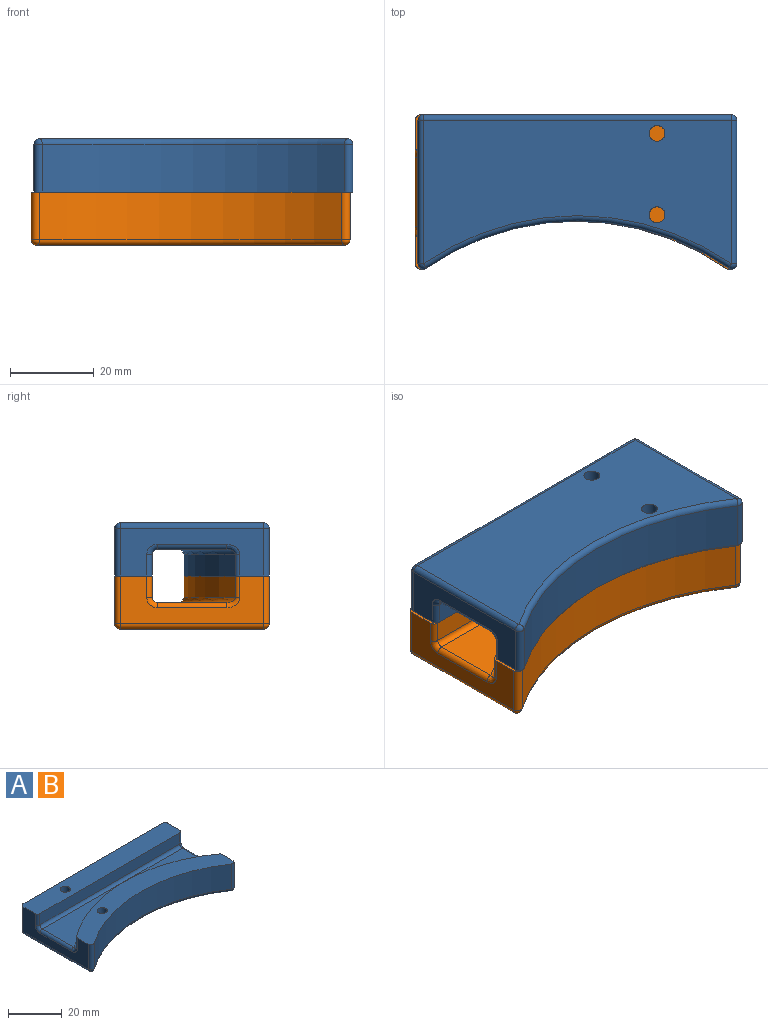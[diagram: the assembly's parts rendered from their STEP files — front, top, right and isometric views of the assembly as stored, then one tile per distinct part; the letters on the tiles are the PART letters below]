
ASSEMBLY  parts=2 mates=1
PART A: 36 faces, bbox 84.1x36.9x12.7 mm
  f0: plane 73.66x16.57mm, normal (0,0,1), area 645.5mm2, adj f13,f14,f18,f19
  f1: plane 73.66x11.43mm, normal (0,1,0), area 841.9mm2, adj f7,f27,f31,f33
  f2: plane 34.35x11.43mm, normal (-1,0,0), area 226.3mm2, adj f7,f9,f10,f11,f14,f15,f17,f24
  f3: cylinder r=63.5mm len=72.22mm, axis (0,0,-1), area 878mm2, adj f9,f22,f24,f25
  f4: plane 34.35x11.43mm, normal (1,0,0), area 226.3mm2, adj f7,f9,f12,f16,f18,f20,f21,f22
  f5: plane 73.66x34.35mm, normal (0,0,-1), area 1932.5mm2, adj f25,f26,f30,f31,f34,f35
  f6: plane 73.66x5.08mm, normal (0,-1,0), area 374.2mm2, adj f7,f15,f19,f21
  f7: plane 76.2x8.89mm, normal (0,0,1), area 664.7mm2, adj f1,f2,f4,f6,f15,f21,f27,f33
  f8: cylinder r=63.5mm len=75.16mm, axis (0,0,-1), area 408.6mm2, adj f9,f10,f12,f13
  f9: plane 76.2x20.38mm, normal (0,0,1), area 663.3mm2, adj f2,f3,f4,f8,f10,f12,f22,f24
  f10: cylinder r=1.27mm len=5.08mm, axis (0,0,-1), area 6mm2, adj f2,f8,f9,f11
  f11: bspline ~3.8x3.03mm, area 5.2mm2, adj f2,f10,f13,f14
  f12: cylinder r=1.27mm len=5.08mm, axis (0,0,-1), area 6mm2, adj f4,f8,f9,f16
  f13: torus R=64.77mm, axis (0,0,1), area 158.9mm2, adj f0,f8,f11,f16
  f14: cylinder r=1.27mm len=16.57mm, axis (0,1,0), area 33.1mm2, adj f0,f2,f11,f17
  f15: cylinder r=1.27mm len=5.08mm, axis (0,0,-1), area 10.1mm2, adj f2,f6,f7,f17
  f16: bspline ~3.98x2.81mm, area 5.2mm2, adj f4,f12,f13,f18
  f17: torus R=2.54mm, axis (1,0,0), area 5.4mm2, adj f2,f14,f15,f19
  f18: cylinder r=1.27mm len=16.57mm, axis (0,-1,0), area 33.1mm2, adj f0,f4,f16,f20
  f19: cylinder r=1.27mm len=73.66mm, axis (1,0,0), area 146.9mm2, adj f0,f6,f17,f20
  f20: torus R=2.54mm, axis (1,0,0), area 5.4mm2, adj f4,f18,f19,f21
  f21: cylinder r=1.27mm len=5.08mm, axis (0,0,1), area 10.1mm2, adj f4,f6,f7,f20
  f22: cylinder r=1.27mm len=11.43mm, axis (0,0,-1), area 31.6mm2, adj f3,f4,f9,f23
  f23: sphere r=1.27mm, area 3.5mm2, adj f22,f25,f26
  f24: cylinder r=1.27mm len=11.43mm, axis (0,0,-1), area 31.6mm2, adj f2,f3,f9,f28
  f25: torus R=64.77mm, axis (0,0,1), area 154.4mm2, adj f3,f5,f23,f28
  f26: cylinder r=1.27mm len=34.35mm, axis (0,1,0), area 68.5mm2, adj f4,f5,f23,f29
  f27: cylinder r=1.27mm len=11.43mm, axis (0,0,-1), area 22.8mm2, adj f1,f4,f7,f29
  f28: sphere r=1.27mm, area 3.5mm2, adj f24,f25,f30
  f29: sphere r=1.27mm, area 2.5mm2, adj f26,f27,f31
  f30: cylinder r=1.27mm len=34.35mm, axis (0,-1,0), area 68.5mm2, adj f2,f5,f28,f32
  f31: cylinder r=1.27mm len=73.66mm, axis (-1,0,0), area 146.9mm2, adj f1,f5,f29,f32
  f32: sphere r=1.27mm, area 2.5mm2, adj f30,f31,f33
  f33: cylinder r=1.27mm len=11.43mm, axis (0,0,1), area 22.8mm2, adj f1,f2,f7,f32
  f34: cylinder r=1.9mm len=12.7mm, axis (0,0,-1), area 151.5mm2, adj f5,f7
  f35: cylinder r=1.9mm len=12.7mm, axis (0,0,-1), area 151.5mm2, adj f5,f9
PART B: same geometry as A
PLACE A rot(axis=(0,1,0),180deg) t=(-2.42,23.32,34.18)mm
PLACE B t=(-3.07,23.32,8.78)mm
MATE fastened A.f7 <-> B.f7  axis (0,0,-1) through (-2.75,18.88,21.48)mm
